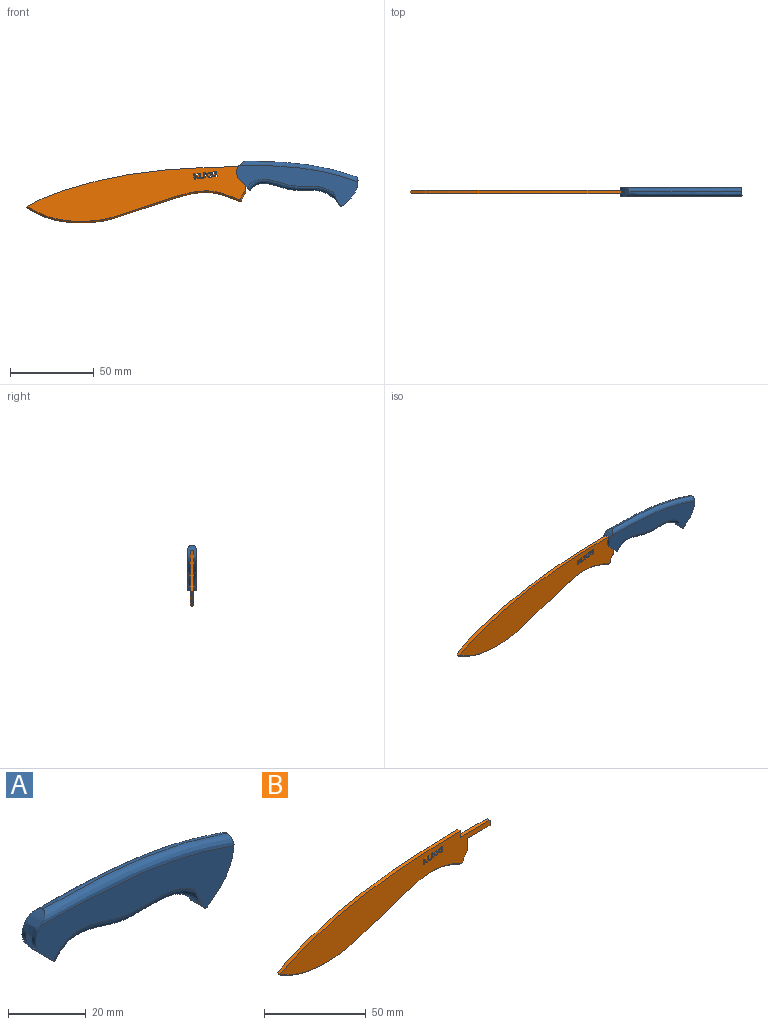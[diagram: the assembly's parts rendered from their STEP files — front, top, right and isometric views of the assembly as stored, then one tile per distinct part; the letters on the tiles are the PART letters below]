
ASSEMBLY  parts=2 mates=1
PART A: 13 faces, bbox 102x5x27.4 mm
  f0: extruded ~17.42x8.08mm, area 83.2mm2, adj f2,f3,f4,f5,f6,f7,f8,f9
  f1: extruded ~17.25x14.59mm, area 126.2mm2, adj f2,f3,f4,f5,f6,f7
  f2: plane 72.71x24.88mm, normal (0,-1,0), area 750.4mm2, adj f0,f1,f4,f6
  f3: plane 72.71x24.88mm, normal (0,1,0), area 750.4mm2, adj f0,f1,f5,f7
  f4: bspline ~102.02x17.6mm, area 274.9mm2, adj f0,f1,f2,f5
  f5: bspline ~78.79x13.78mm, area 274.9mm2, adj f0,f1,f3,f4
  f6: bspline ~57.32x15.39mm, area 218.5mm2, adj f0,f1,f2,f7
  f7: bspline ~57.32x15.39mm, area 218.5mm2, adj f0,f1,f3,f6
  f8: plane 29.35x5.93mm, normal (0,-1,0), area 166.6mm2, adj f0,f9,f11,f12
  f9: plane 29.24x2mm, normal (0,0,-1), area 58.5mm2, adj f0,f8,f10,f12
  f10: plane 29.35x5.93mm, normal (0,1,0), area 166.6mm2, adj f0,f9,f11,f12
  f11: plane 26.96x2mm, normal (0,0,1), area 53.9mm2, adj f0,f8,f10,f12
  f12: plane 5.83x2mm, normal (-1,0,0), area 11.7mm2, adj f8,f9,f10,f11
PART B: 59 faces, bbox 149.4x2.6x34.2 mm
  f0: extruded ~3.17x2mm, area 8.6mm2, adj f1,f52,f53,f54
  f1: plane 2x1.88mm, normal (1,0,0), area 3.8mm2, adj f0,f2,f53,f54
  f2: plane 2x0.63mm, normal (0,0,-1), area 1.3mm2, adj f1,f3,f53,f54
  f3: plane 2x1.88mm, normal (-1,0,0), area 3.8mm2, adj f2,f4,f53,f54
  f4: extruded ~2x1.98mm, area 5mm2, adj f3,f52,f53,f54
  f5: plane 3.18x2mm, normal (1,0,0.06), area 6.4mm2, adj f6,f47,f53,f54
  f6: plane 2x0.73mm, normal (0,0,-1), area 1.5mm2, adj f5,f7,f53,f54
  f7: plane 3.13x2mm, normal (-1,0,-0.06), area 6.3mm2, adj f6,f47,f53,f54
  f8: plane 2x0.53mm, normal (-0.06,0,1), area 1.1mm2, adj f9,f48,f53,f54
  f9: plane 2.34x2mm, normal (1,0,0.06), area 4.7mm2, adj f8,f10,f53,f54
  f10: plane 2.38x2mm, normal (0.06,0,-1), area 4.8mm2, adj f9,f11,f53,f54
  f11: extruded ~2x0.24mm, area 1.1mm2, adj f10,f12,f53,f54
  f12: plane 2.35x2mm, normal (-0.06,0,1), area 4.7mm2, adj f11,f13,f53,f54
  f13: plane 2x0.43mm, normal (1,0,0.06), area 0.9mm2, adj f12,f14,f53,f54
  f14: plane 2.7x2mm, normal (0.06,0,-1), area 5.4mm2, adj f13,f15,f53,f54
  f15: extruded ~2x1.02mm, area 2.6mm2, adj f14,f16,f53,f54
  f16: plane 2x1.17mm, normal (0,0,1), area 2.3mm2, adj f15,f17,f53,f54
  f17: extruded ~2x1.59mm, area 4.8mm2, adj f16,f18,f53,f54
  f18: plane 2x0.5mm, normal (-1,0,-0.05), area 1mm2, adj f17,f19,f53,f54
  f19: extruded ~2.2x2mm, area 6mm2, adj f18,f20,f53,f54
  f20: plane 2x0.45mm, normal (-0.11,0,0.99), area 0.9mm2, adj f19,f48,f53,f54
  f21: extruded ~3.18x2mm, area 6.4mm2, adj f22,f49,f53,f54
  f22: plane 2x0.44mm, normal (0,0,-1), area 0.9mm2, adj f21,f23,f53,f54
  f23: plane 2x0.53mm, normal (-1,0,0), area 1.1mm2, adj f22,f24,f53,f54
  f24: plane 2.38x2mm, normal (0.32,0,-0.95), area 5mm2, adj f23,f25,f53,f54
  f25: plane 2x0.59mm, normal (-1,0,0), area 1.2mm2, adj f24,f26,f53,f54
  f26: plane 2x1.17mm, normal (-0.33,0,0.94), area 2.5mm2, adj f25,f27,f53,f54
  f27: extruded ~2x1.74mm, area 5.3mm2, adj f26,f28,f53,f54
  f28: extruded ~2.76x2.16mm, area 12.4mm2, adj f27,f49,f53,f54
  f29: extruded ~126.01x24.24mm, area 258.3mm2, adj f30,f50,f53,f54,f55,f58
  f30: extruded ~52.71x9.35mm, area 8.6mm2, adj f29,f31,f55,f58
  f31: extruded ~78.13x15.37mm, area 13.2mm2, adj f30,f32,f56,f57
  f32: plane 8.66x2.01mm, normal (1,0,0), area 16.2mm2, adj f31,f33,f53,f54,f56,f57
  f33: plane 15.72x2mm, normal (0,0,-1), area 31.4mm2, adj f32,f34,f53,f54
  f34: plane 3.12x2mm, normal (1,0,0), area 6.2mm2, adj f33,f35,f53,f54
  f35: plane 20.55x2mm, normal (0,0,1), area 41.1mm2, adj f34,f50,f53,f54
  f36: plane 2x0.37mm, normal (0,0,1), area 0.7mm2, adj f37,f51,f53,f54
  f37: plane 2.82x2mm, normal (1,0,0.09), area 5.7mm2, adj f36,f38,f53,f54
  f38: plane 2x0.41mm, normal (0.45,0,-0.89), area 0.9mm2, adj f37,f39,f53,f54
  f39: plane 2x0.68mm, normal (-1,0,0), area 1.4mm2, adj f38,f40,f53,f54
  f40: plane 2.56x2mm, normal (0.32,0,-0.95), area 5.4mm2, adj f39,f41,f53,f54
  f41: plane 2x0.5mm, normal (-0.96,0,0.28), area 1mm2, adj f40,f42,f53,f54
  f42: plane 2x1.26mm, normal (-0.33,0,0.94), area 2.7mm2, adj f41,f43,f53,f54
  f43: extruded ~2x1.81mm, area 5.2mm2, adj f42,f44,f53,f54
  f44: plane 2x0.42mm, normal (-0.99,0,0.17), area 0.8mm2, adj f43,f45,f53,f54
  f45: extruded ~2x2mm, area 6.2mm2, adj f44,f46,f53,f54
  f46: plane 2x0.5mm, normal (-0.47,0,0.88), area 1.1mm2, adj f45,f51,f53,f54
  f47: plane 2x0.73mm, normal (-0.06,0,1), area 1.5mm2, adj f5,f7,f53,f54
  f48: plane 2x1.8mm, normal (-0.99,0,-0.11), area 3.6mm2, adj f8,f20,f53,f54
  f49: plane 2x0.64mm, normal (0,0,1), area 1.3mm2, adj f21,f28,f53,f54
  f50: plane 3.85x2mm, normal (1,0,0), area 7.7mm2, adj f29,f35,f53,f54
  f51: plane 2x1.76mm, normal (-1,0,0), area 3.5mm2, adj f36,f46,f53,f54
  f52: extruded ~2.16x2mm, area 9.3mm2, adj f0,f4,f53,f54
  f53: plane 146.54x33.44mm, normal (0,-1,0), area 2317.1mm2, adj f0,f1,f2,f3,f4,f5,f6,f7
  f54: plane 146.53x33.44mm, normal (0,1,0), area 2317.4mm2, adj f0,f1,f2,f3,f4,f5,f6,f7
  f55: bspline ~52.71x10.12mm, area 70.7mm2, adj f29,f30,f54,f56
  f56: bspline ~79.37x16.58mm, area 109.6mm2, adj f31,f32,f54,f55
  f57: bspline ~79.37x16.58mm, area 110.4mm2, adj f31,f32,f53,f58
  f58: bspline ~54.95x11.66mm, area 70.7mm2, adj f29,f30,f53,f57
PLACE A t=(-13.17,27.81,-7.22)mm
PLACE B t=(-16.89,26.31,-13.51)mm
MATE slider B.f34 <-> A.f12  axis (1,0,0) through (33.4,25.31,6.08)mm
